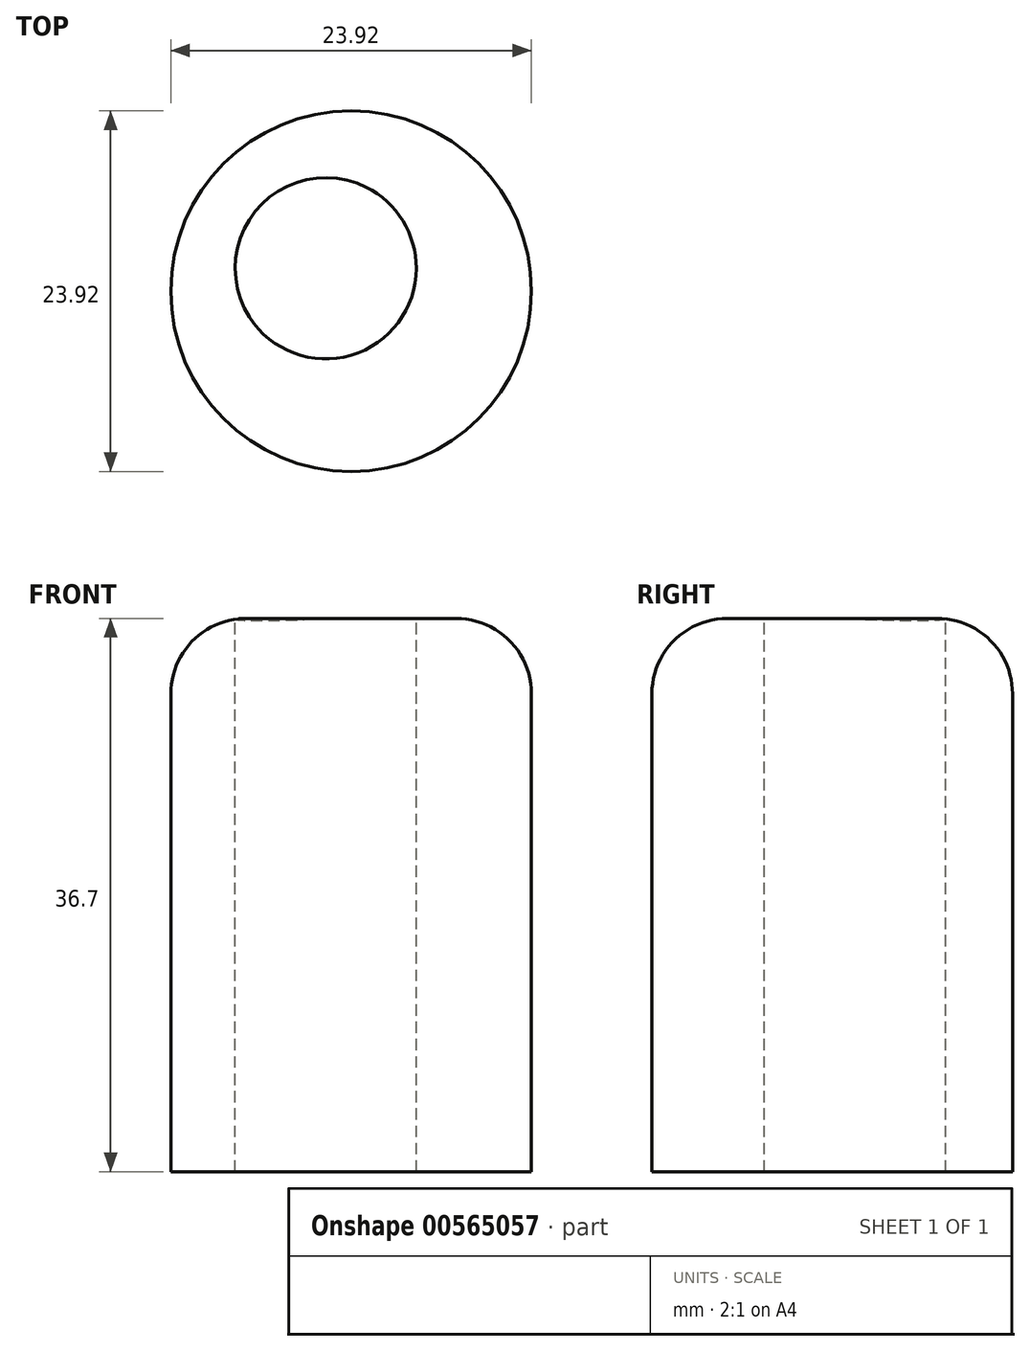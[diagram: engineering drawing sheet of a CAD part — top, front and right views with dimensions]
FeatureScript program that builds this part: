
annotation { "Feature Type Name" : "Feature", "Feature Type Description" : "" }
export const myFeature = defineFeature(function(context is Context, id is Id, definition is map)
    precondition{}
    {
        {
            var Q0;
            Q0=qCreatedBy(makeId("Top.planeOp"),FACE);
            var sketch = newSketch(context, id + "F0", { "sketchPlane" : qUnion([Q0])});
            skCircle(sketch, "E0", {"center": v(0, 0) * mm, "radius": 11.96 * mm});
            skSolve(sketch);
        }
        {
            var Q0;
            Q0 = qSketchRegion(id + "F0", true);
            extrude(context, id + "F1", {"entities" : qUnion([Q0]), "depth" : 36.7 * mm, "offsetDistance" : 25 * mm});
        }
        {
            var Q0;
            Q0=makeQuery(id+"F1.opExtrude","CAP_FACE",FACE,{"disambiguationData":[OSD([sQuery(id+"F0.wireOp",EDGE,"E0")])],"isStart":false});
            var sketch = newSketch(context, id + "F2", { "sketchPlane" : qUnion([Q0])});
            skCircle(sketch, "E1", {"center": v(-1.68, 1.52) * mm, "radius": 6 * mm});
            skSolve(sketch);
        }
        {
            var Q0;
            Q0 = qSketchRegion(id + "F2", true);
            extrude(context, id + "F3", {"entities" : qUnion([Q0]), "operationType" : NewBodyOperationType.REMOVE, "endBound" : BoundingType.THROUGH_ALL, "oppositeDirection" : true, "depth" : 25 * mm, "offsetDistance" : 25 * mm});
        }
        {
            var Q0;
            Q0=makeQuery(id+"F1.opExtrude","CAP_EDGE",EDGE,{"disambiguationData":[OSD([sQuery(id+"F0.wireOp",EDGE,"E0")])],"isStart":false});
            fillet(context, id + "F4", {"entities" : qUnion([Q0]), "radius" : 5 * mm, "tangentPropagation" : true, "allowEdgeOverflow" : false});
        }
    });
